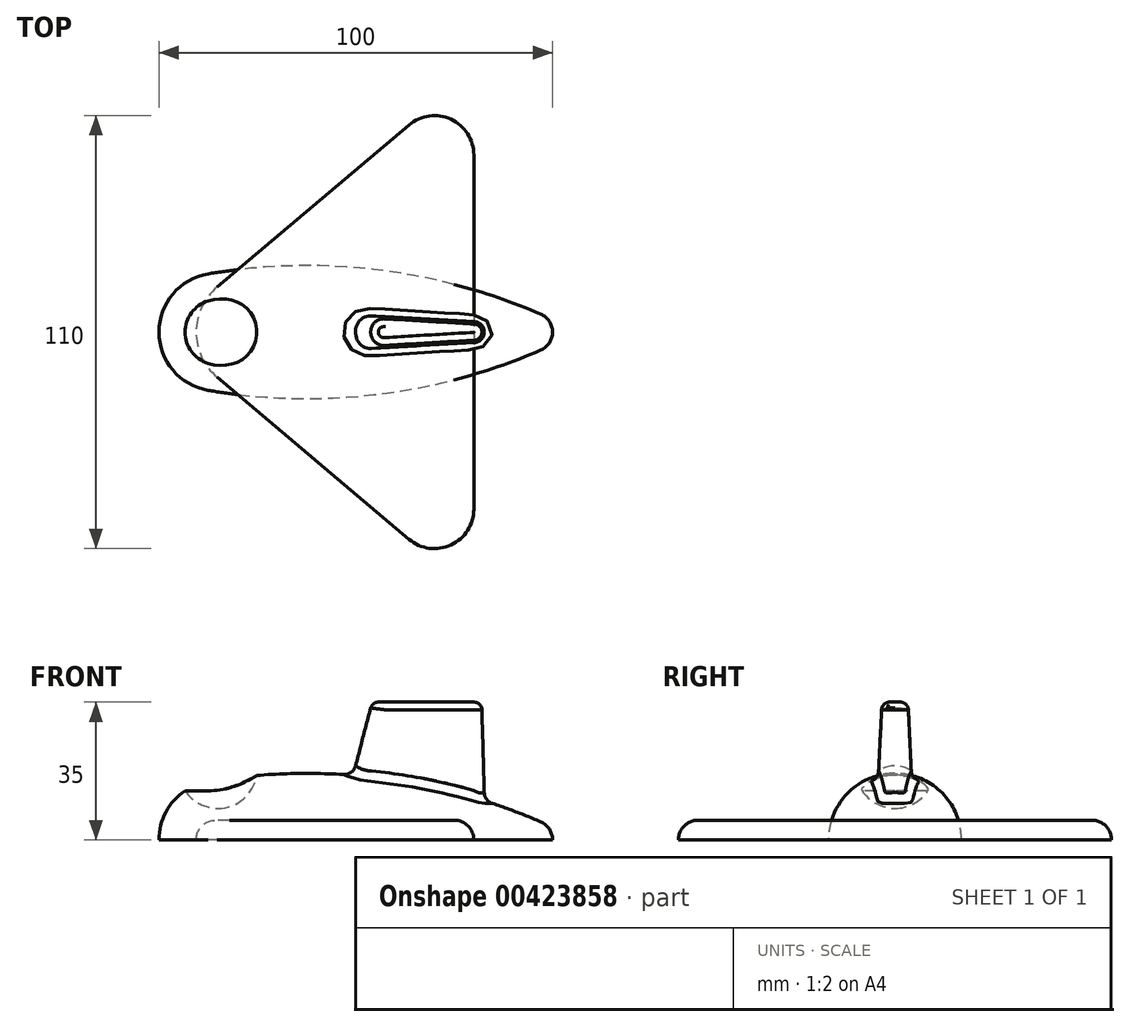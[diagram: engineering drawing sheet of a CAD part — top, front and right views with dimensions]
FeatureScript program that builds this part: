
annotation { "Feature Type Name" : "Feature", "Feature Type Description" : "" }
export const myFeature = defineFeature(function(context is Context, id is Id, definition is map)
    precondition{}
    {
        {
            var Q0;
            Q0=qCreatedBy(makeId("Top.planeOp"),FACE);
            var sketch = newSketch(context, id + "F0", { "sketchPlane" : qUnion([Q0])});
            skArc(sketch, "E0", {"start": v(-2.5, 14.8) * mm, "mid": v(-11.46, 9.68) * mm, "end": v(-15, 0) * mm});
            skLineSegment(sketch, "E1", {"start": v(-15, 0) * mm, "end": v(85, 0) * mm});
            skArc(sketch, "E2", {"start": v(85, 0) * mm, "mid": v(84.18, 2.75) * mm, "end": v(81.98, 4.6) * mm});
            skArc(sketch, "E3", {"start": v(81.98, 4.6) * mm, "mid": v(40.48, 15.8) * mm, "end": v(-2.5, 14.8) * mm});
            skSolve(sketch);
        }
        {
            var Q0;
            Q0=makeQuery(id+"F0.imprint","IMPRINT",FACE,{"disambiguationData":[TD([[makeQuery(id+"F0.imprint","IMPRINT",EDGE,{"derivedFrom":sQuery(id+"F0.wireOp",EDGE,"E0")}),1.0]])]});
            var Q1;
            Q1=sQuery(id+"F0.wireOp",EDGE,"E1");
            revolve(context, id + "F1", {"entities" : qUnion([Q0]), "axis" : qUnion([Q1]), "revolveType" : RevolveType.ONE_DIRECTION, "angle" : 180 * degree});
        }
        {
            var Q0;
            Q0=qCreatedBy(makeId("Top.planeOp"),FACE);
            var sketch = newSketch(context, id + "F2", { "sketchPlane" : qUnion([Q0])});
            skArc(sketch, "E4", {"start": v(35.33, 4.99) * mm, "mid": v(31.58, 3.65) * mm, "end": v(30, 0) * mm});
            skArc(sketch, "E5", {"start": v(68, 0) * mm, "mid": v(67.2, 2.05) * mm, "end": v(65.2, 3) * mm});
            skLineSegment(sketch, "E6", {"start": v(35.33, 4.99) * mm, "end": v(65.2, 3) * mm});
            skArc(sketch, "E7.MirrorCS", {"start": v(68, 0) * mm, "mid": v(67.2, -2.05) * mm, "end": v(65.2, -3) * mm});
            skLineSegment(sketch, "E8.MirrorCS", {"start": v(35.33, -4.99) * mm, "end": v(65.2, -3) * mm});
            skArc(sketch, "E9.MirrorCS", {"start": v(35.33, -4.99) * mm, "mid": v(31.58, -3.65) * mm, "end": v(30, 0) * mm});
            skSolve(sketch);
        }
        {
            var Q0;
            Q0=qCreatedBy(makeId("Top.planeOp"),FACE);
            cPlane(context, id + "F3", {"entities" : qUnion([Q0]), "cplaneType" : CPlaneType.OFFSET, "offset" : 35 * mm, "width" : 150 * mm, "height" : 150 * mm});
        }
        {
            var Q0;
            Q0=qCreatedBy(id+"F3.planeOp",FACE);
            var sketch = newSketch(context, id + "F4", { "sketchPlane" : qUnion([Q0])});
            skArc(sketch, "E10", {"start": v(42.7, 3.3) * mm, "mid": v(40.23, 2.4) * mm, "end": v(39.2, 0) * mm});
            skArc(sketch, "E11", {"start": v(67, 0) * mm, "mid": v(66.45, 1.37) * mm, "end": v(65.12, 2) * mm});
            skLineSegment(sketch, "E12", {"start": v(42.7, 3.3) * mm, "end": v(65.12, 2) * mm});
            skArc(sketch, "E13.MirrorCS", {"start": v(67, 0) * mm, "mid": v(66.45, -1.37) * mm, "end": v(65.12, -2) * mm});
            skLineSegment(sketch, "E14.MirrorCS", {"start": v(42.7, -3.3) * mm, "end": v(65.12, -2) * mm});
            skArc(sketch, "E15.MirrorCS", {"start": v(42.7, -3.3) * mm, "mid": v(40.23, -2.4) * mm, "end": v(39.2, 0) * mm});
            skSolve(sketch);
        }
        {
            var Q1;
            Q1 = qSketchRegion(id + "F2", true);
            var Q2;
            Q2 = qSketchRegion(id + "F4", true);
            loft(context, id + "F5", {"operationType" : NewBodyOperationType.ADD, "sheetProfilesArray" : [{ "sheetProfileEntities" : qUnion([Q1]) }, { "sheetProfileEntities" : qUnion([Q2]) }]});
        }
        {
            var Q0;
            Q0=makeQuery(id+"F5.opLoft","MID_CAP_EDGE",EDGE,{"disambiguationData":[OSD([sQuery(id+"F4.wireOp",EDGE,"E13.MirrorCS"),sQuery(id+"F4.wireOp",EDGE,"E14.MirrorCS"),sQuery(id+"F4.wireOp",EDGE,"E15.MirrorCS")])],"capPos":1.0});
            var Q1;
            Q1=makeQuery(id+"F5.opLoft","MID_CAP_EDGE",EDGE,{"disambiguationData":[OSD([sQuery(id+"F4.wireOp",EDGE,"E10"),sQuery(id+"F4.wireOp",EDGE,"E14.MirrorCS"),sQuery(id+"F4.wireOp",EDGE,"E15.MirrorCS")])],"capPos":1.0});
            var Q2;
            Q2=makeQuery(id+"F5.opLoft","MID_CAP_EDGE",EDGE,{"disambiguationData":[OSD([sQuery(id+"F4.wireOp",EDGE,"E10"),sQuery(id+"F4.wireOp",EDGE,"E12"),sQuery(id+"F4.wireOp",EDGE,"E15.MirrorCS")])],"capPos":1.0});
            var Q3;
            Q3=makeQuery(id+"F5.opLoft","MID_CAP_EDGE",EDGE,{"disambiguationData":[OSD([sQuery(id+"F4.wireOp",EDGE,"E10"),sQuery(id+"F4.wireOp",EDGE,"E11"),sQuery(id+"F4.wireOp",EDGE,"E12")])],"capPos":1.0});
            var Q4;
            Q4=makeQuery(id+"F5.opLoft","MID_CAP_EDGE",EDGE,{"disambiguationData":[OSD([sQuery(id+"F4.wireOp",EDGE,"E11"),sQuery(id+"F4.wireOp",EDGE,"E12"),sQuery(id+"F4.wireOp",EDGE,"E13.MirrorCS")])],"capPos":1.0});
            fillet(context, id + "F6", {"entities" : qUnion([Q0, Q1, Q2, Q3, Q4]), "radius" : 2 * mm, "tangentPropagation" : true, "allowEdgeOverflow" : false});
        }
        {
            var Q0;
            Q0=qCreatedBy(makeId("Front.planeOp"),FACE);
            var sketch = newSketch(context, id + "F7", { "sketchPlane" : qUnion([Q0])});
            skArc(sketch, "E16", {"start": v(0, 8) * mm, "mid": v(10, 18) * mm, "end": v(0, 28) * mm});
            skLineSegment(sketch, "E17", {"start": v(0, 28) * mm, "end": v(0, 8) * mm});
            skPoint(sketch, "E18.orphan", {"position": v(0, 32.24) * mm});
            skSolve(sketch);
        }
        {
            var Q0;
            Q0=makeQuery(id+"F7.imprint","IMPRINT",FACE,{"disambiguationData":[TD([[makeQuery(id+"F7.imprint","IMPRINT",EDGE,{"derivedFrom":sQuery(id+"F7.wireOp",EDGE,"E16")}),1.0]])]});
            var Q1;
            Q1=sQuery(id+"F7.wireOp",EDGE,"E17");
            revolve(context, id + "F8", {"operationType" : NewBodyOperationType.REMOVE, "entities" : qUnion([Q0]), "axis" : qUnion([Q1]), "revolveType" : RevolveType.FULL, "oppositeDirection" : true});
        }
        {
            var Q0;
            Q0=qCreatedBy(makeId("Top.planeOp"),FACE);
            var sketch = newSketch(context, id + "F9", { "sketchPlane" : qUnion([Q0])});
            skLineSegment(sketch, "E19", {"start": v(-0.21, 11.46) * mm, "end": v(48.55, 52.64) * mm});
            skLineSegment(sketch, "E20", {"start": v(65, 45) * mm, "end": v(65, 0) * mm});
            skPoint(sketch, "E21.orphan", {"position": v(-2.5, 14.8) * mm});
            skPoint(sketch, "E22.visualSharp", {"position": v(65, 66.53) * mm});
            skArc(sketch, "E22.filletArc", {"start": v(65, 45) * mm, "mid": v(59.21, 54.07) * mm, "end": v(48.55, 52.64) * mm});
            skLineSegment(sketch, "E23.MirrorCS", {"start": v(65, -45) * mm, "end": v(65, 0) * mm});
            skArc(sketch, "E24.MirrorCS", {"start": v(65, -45) * mm, "mid": v(59.21, -54.07) * mm, "end": v(48.55, -52.64) * mm});
            skLineSegment(sketch, "E25.MirrorCS", {"start": v(-0.21, -11.46) * mm, "end": v(48.55, -52.64) * mm});
            skPoint(sketch, "E26.newPointA", {"position": v(-5.43, 7.06) * mm});
            skPoint(sketch, "E26.newPointB", {"position": v(-5.43, -7.06) * mm});
            skArc(sketch, "E26.filletArc", {"start": v(-0.21, 11.46) * mm, "mid": v(-5.54, 0) * mm, "end": v(-0.21, -11.46) * mm});
            skSolve(sketch);
        }
        {
            var Q0;
            {var subQ0=sQuery(id+"F9.wireOp",EDGE,"E23.MirrorCS");Q0=makeQuery(id+"F9.imprint","IMPRINT",FACE,{"disambiguationData":[TD([[makeQuery(id+"F9.imprint","IMPRINT",EDGE,{"derivedFrom":subQ0}),1.0]])]});}
            extrude(context, id + "F10", {"entities" : qUnion([Q0]), "depth" : 5 * mm});
        }
        {
            var Q0;
            Q0=makeQuery(id+"F10.opExtrude","CAP_FACE",FACE,{"disambiguationData":[OSD([sQuery(id+"F9.wireOp",EDGE,"E19"),sQuery(id+"F9.wireOp",EDGE,"E20"),sQuery(id+"F9.wireOp",EDGE,"E22.filletArc"),sQuery(id+"F9.wireOp",EDGE,"E23.MirrorCS"),sQuery(id+"F9.wireOp",EDGE,"E24.MirrorCS"),sQuery(id+"F9.wireOp",EDGE,"E25.MirrorCS"),sQuery(id+"F9.wireOp",EDGE,"E26.filletArc")])],"isStart":false});
            fillet(context, id + "F11", {"entities" : qUnion([Q0]), "radius" : 5 * mm, "tangentPropagation" : true, "allowEdgeOverflow" : false});
        }
        {
            var Q0;
            Q0=makeQuery(id+"F5.boolean.opBoolean","INTERSECT",EDGE,{"derivedFrom":[makeQuery(id+"F1.opRevolve","SWEPT_FACE",FACE,{"disambiguationData":[OSD([sQuery(id+"F0.wireOp",EDGE,"E3")])]}),makeQuery(id+"F5.opLoft","SWEPT_FACE",FACE,{"disambiguationData":[OSD([sQuery(id+"F2.wireOp",EDGE,"E4"),sQuery(id+"F2.wireOp",EDGE,"E6"),sQuery(id+"F2.wireOp",EDGE,"E9.MirrorCS"),sQuery(id+"F4.wireOp",EDGE,"E10"),sQuery(id+"F4.wireOp",EDGE,"E12"),sQuery(id+"F4.wireOp",EDGE,"E15.MirrorCS")])]})]});
            fillet(context, id + "F12", {"entities" : qUnion([Q0]), "radius" : 3 * mm, "tangentPropagation" : true, "allowEdgeOverflow" : false});
        }
    });
